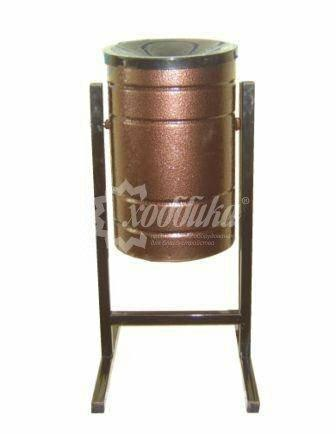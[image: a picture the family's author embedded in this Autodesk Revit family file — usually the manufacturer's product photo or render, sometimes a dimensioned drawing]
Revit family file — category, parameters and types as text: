
# Revit family: Урна-пепельница Омега Арт 7331
name_source: partatom
category: Антураж
revit_build: Autodesk Revit 2018 (Build: 20180423_1000(x64)
units: mm (PartAtom-declared; Revit-internal decimal feet)

## family parameters
Всегда вертикально = Да
Источник визуального образа = Геометрия семейства
На основе рабочей плоскости = Нет
Общий = Нет
При загрузке вырезать с полостями = Нет
Точка расчета площади = Нет

## types (2) — shared parameters
URL = https://hobbyka.ru
Артикул товара = Арт. 7331
Высота = 620 мм
Группа модели = Уличные урны
Длина = 360 мм
Изготовитель = ООО «Хоббика»
Материал изделия = Сталь
Цвет опор = Опора
Цвет урны = Урна
Ширина = 300 мм

## per-type parameters (varying)
| type | Изображение типоразмера | Объем 20 литров | Объем 30 литров | Описание |
| Объем 20 литров | Урна-пепельница Омега Арт 7331 20 литров.jpg | Да | Нет | Урна-пепельница Омега, объемом 20 литров |
| Объем 30 литров | Урна-пепельница Омега Арт 7331 30 литров.jpg | Нет | Да | Урна-пепельница Омега, объемом 30 литров |
